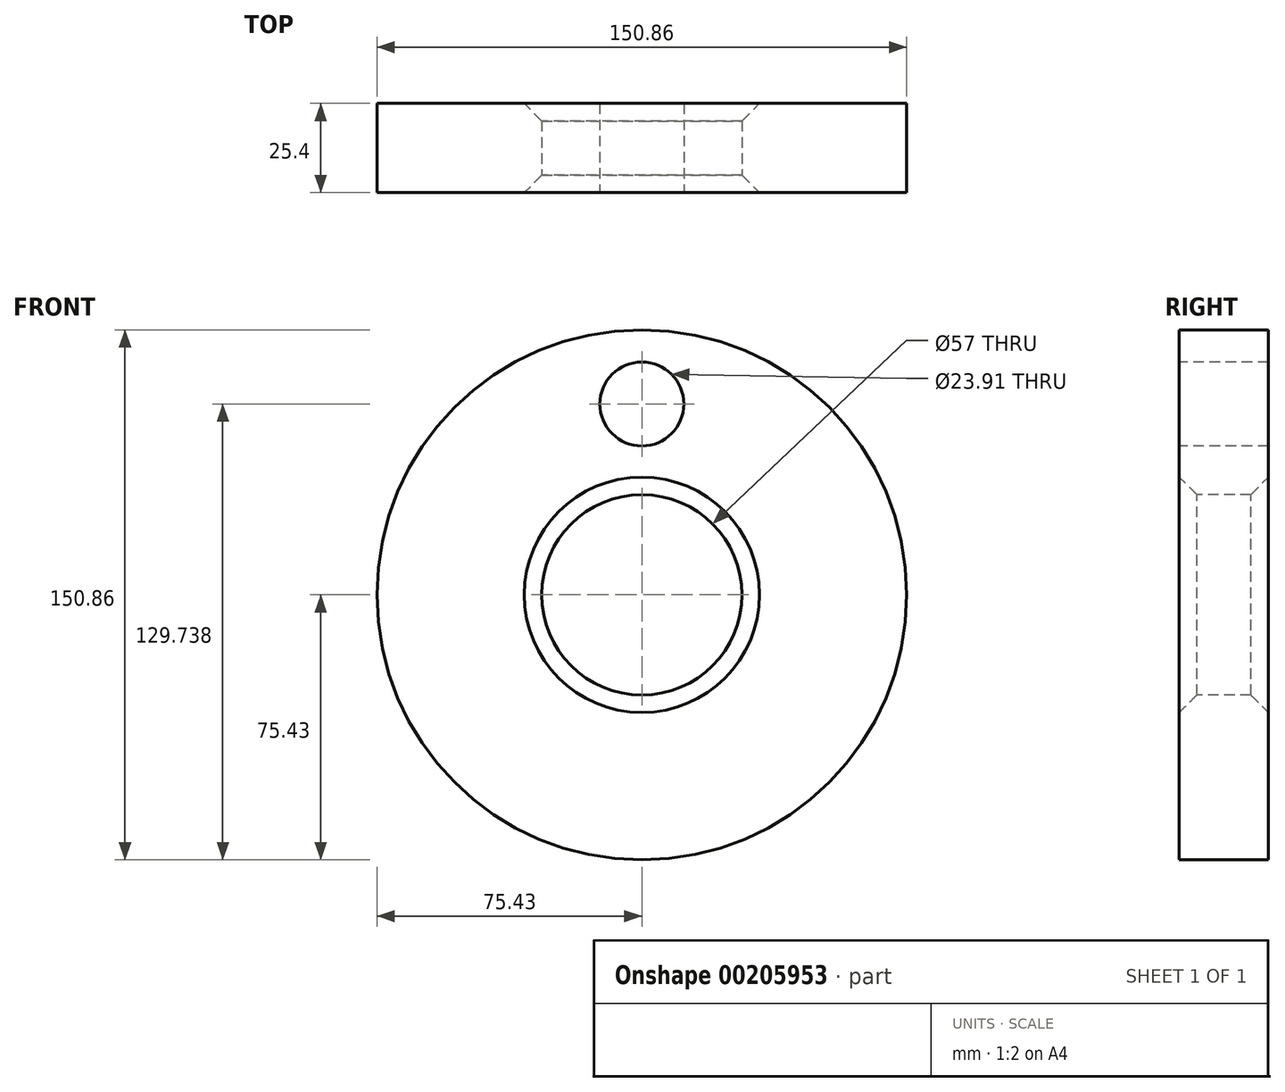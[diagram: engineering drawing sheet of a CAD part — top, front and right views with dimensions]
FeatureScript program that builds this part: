
annotation { "Feature Type Name" : "Feature", "Feature Type Description" : "" }
export const myFeature = defineFeature(function(context is Context, id is Id, definition is map)
    precondition{}
    {
        {
            var Q0;
            Q0=qCreatedBy(makeId("Front.planeOp"),FACE);
            var sketch = newSketch(context, id + "F0", { "sketchPlane" : qUnion([Q0])});
            skCircle(sketch, "E0", {"center": v(0, 0) * mm, "radius": 75.43 * mm});
            skSolve(sketch);
        }
        {
            var Q0;
            Q0=makeQuery(id+"F0.imprint","IMPRINT",FACE,{"disambiguationData":[TD([[makeQuery(id+"F0.imprint","IMPRINT",EDGE,{"derivedFrom":sQuery(id+"F0.wireOp",EDGE,"E0")}),1.0]])]});
            extrude(context, id + "F1", {"entities" : qUnion([Q0]), "depth" : 25.4 * mm});
        }
        {
            var Q0;
            Q0=makeQuery(id+"F1.opExtrude","CAP_FACE",FACE,{"disambiguationData":[OSD([sQuery(id+"F0.wireOp",EDGE,"E0")])],"isStart":false});
            var sketch = newSketch(context, id + "F2", { "sketchPlane" : qUnion([Q0])});
            skCircle(sketch, "E1", {"center": v(0, 0) * mm, "radius": 25.37 * mm});
            skSolve(sketch);
        }
        {
            var Q0;
            Q0=makeQuery(id+"F1.opExtrude","CAP_FACE",FACE,{"disambiguationData":[OSD([sQuery(id+"F0.wireOp",EDGE,"E0")])],"isStart":false});
            var sketch = newSketch(context, id + "F3", { "sketchPlane" : qUnion([Q0])});
            skCircle(sketch, "E2", {"center": v(0, 0) * mm, "radius": 28.5 * mm});
            skSolve(sketch);
        }
        {
            var Q0;
            Q0=makeQuery(id+"F2.imprint","IMPRINT",FACE,{"disambiguationData":[TD([[makeQuery(id+"F2.imprint","IMPRINT",EDGE,{"derivedFrom":sQuery(id+"F2.wireOp",EDGE,"E1")}),1.0]])]});
            var Q1;
            Q1=makeQuery(id+"F3.imprint","IMPRINT",FACE,{"disambiguationData":[TD([[makeQuery(id+"F3.imprint","IMPRINT",EDGE,{"derivedFrom":sQuery(id+"F3.wireOp",EDGE,"E2")}),1.0]])]});
            var Q2;
            Q2=sQuery(id+"F2.wireOp",EDGE,"E1");
            extrude(context, id + "F4", {"entities" : qUnion([Q0, Q1]), "operationType" : NewBodyOperationType.REMOVE, "surfaceEntities" : qUnion([Q2]), "oppositeDirection" : true, "depth" : 80.5 * mm});
        }
        {
            var Q0;
            Q0=makeQuery(id+"F4.boolean.opBoolean","COPY",EDGE,{"derivedFrom":makeQuery(id+"F4.opExtrude","CAP_EDGE",EDGE,{"disambiguationData":[OSD([sQuery(id+"F3.wireOp",EDGE,"E2")])],"isStart":true})});
            var Q1;
            Q1=makeQuery(id+"F4.boolean.opBoolean","COPY",FACE,{"derivedFrom":makeQuery(id+"F4.opExtrude","SWEPT_FACE",FACE,{"disambiguationData":[OSD([sQuery(id+"F3.wireOp",EDGE,"E2")])]})});
            chamfer(context, id + "F6", {"entities" : qUnion([Q0, Q1]), "width" : 5 * mm, "tangentPropagation" : true});
        }
        {
            var Q0;
            Q0=makeQuery(id+"F1.opExtrude","CAP_FACE",FACE,{"disambiguationData":[OSD([sQuery(id+"F0.wireOp",EDGE,"E0")])],"isStart":false});
            var sketch = newSketch(context, id + "F7", { "sketchPlane" : qUnion([Q0])});
            skCircle(sketch, "E3", {"center": v(0, 54.3) * mm, "radius": 11.96 * mm});
            skSolve(sketch);
        }
        {
            var Q0;
            Q0=makeQuery(id+"F7.imprint","IMPRINT",FACE,{"disambiguationData":[TD([[makeQuery(id+"F7.imprint","IMPRINT",EDGE,{"derivedFrom":sQuery(id+"F7.wireOp",EDGE,"E3")}),1.0]])]});
            extrude(context, id + "F5", {"entities" : qUnion([Q0]), "operationType" : NewBodyOperationType.REMOVE, "endBound" : BoundingType.THROUGH_ALL, "oppositeDirection" : true, "depth" : 25 * mm});
        }
    });
